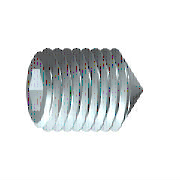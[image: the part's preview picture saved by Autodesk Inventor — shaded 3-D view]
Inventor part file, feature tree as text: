
AUTODESK INVENTOR PART (.ipt)
format: ipt  version: 2020 (Build 240168000, 168)  size: 165,888 bytes
history: native  units: mm (DEFAULTED — no unit token found)
features: sketch x2, extrude x1, other x1, plane x1
ambient origin geometry x8: Origin, YZ Plane, XZ Plane, XY Plane, X Axis, Y Axis, Z Axis, Center Point
bodies: Solid1 (feature_tree), Body (feature_tree)
feature tree (5):
  extrude  "Slot"  TaperAngle=60.0deg  [1 undecoded]
  other  "Work Axis1"
  plane  "Work Plane1"
  sketch  "Sketch1"  dims[d0=3.0mm d1=60.0deg]
  sketch  "Sketch2"  dims[d2=5.0mm d3=2.886751mm d6=90.0deg d4=0.0mm d5=10.0mm d21=10.0mm d7=0.0mm d8=2.499995mm d9=45.0deg d10=0.49076mm d11=45.0deg d12=10.0mm d13=0.0mm d34=2.499995mm d35=0.49076mm d36=0.0mm d37=0.0mm]
note: 1 required parameter value undecoded (feature->parameter linkage not recoverable at this tier; creation-order binding heuristic only, values carry confidence <= 0.55)
